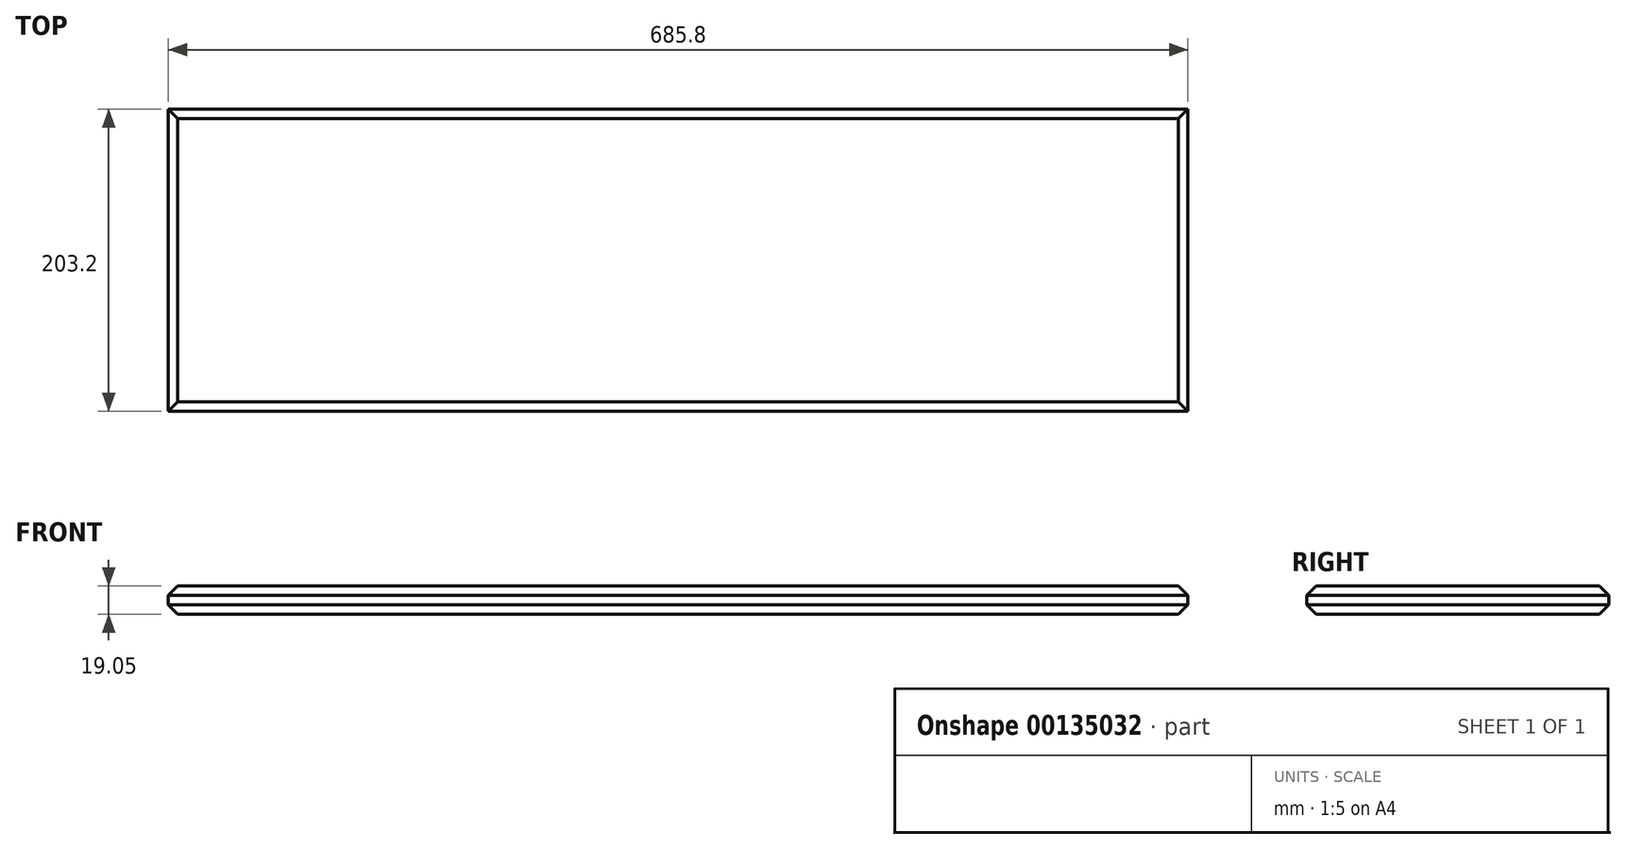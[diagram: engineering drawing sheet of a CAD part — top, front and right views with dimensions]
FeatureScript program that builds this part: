
annotation { "Feature Type Name" : "Feature", "Feature Type Description" : "" }
export const myFeature = defineFeature(function(context is Context, id is Id, definition is map)
    precondition{}
    {
        {
            var Q0;
            Q0=qCreatedBy(makeId("Top.planeOp"),FACE);
            var sketch = newSketch(context, id + "F0", { "sketchPlane" : qUnion([Q0])});
            skLineSegment(sketch, "E0.bottom", {"start": v(-467.83, 102.3) * mm, "end": v(217.97, 102.3) * mm});
            skLineSegment(sketch, "E0.top", {"start": v(-467.83, -100.9) * mm, "end": v(217.97, -100.9) * mm});
            skLineSegment(sketch, "E0.left", {"start": v(-467.83, 102.3) * mm, "end": v(-467.83, -100.9) * mm});
            skLineSegment(sketch, "E0.right", {"start": v(217.97, 102.3) * mm, "end": v(217.97, -100.9) * mm});
            skSolve(sketch);
        }
        {
            var Q0;
            Q0=makeQuery(id+"F0.imprint","IMPRINT",FACE,{"disambiguationData":[TD([[makeQuery(id+"F0.imprint","IMPRINT",EDGE,{"derivedFrom":sQuery(id+"F0.wireOp",EDGE,"E0.bottom")}),-1.0]])]});
            extrude(context, id + "F1", {"entities" : qUnion([Q0]), "depth" : 19.05 * mm});
        }
        {
            var Q0;
            Q0=makeQuery(id+"F1.opExtrude","CAP_FACE",FACE,{"disambiguationData":[OSD([sQuery(id+"F0.wireOp",EDGE,"E0.bottom"),sQuery(id+"F0.wireOp",EDGE,"E0.top"),sQuery(id+"F0.wireOp",EDGE,"E0.left"),sQuery(id+"F0.wireOp",EDGE,"E0.right")])],"isStart":false});
            chamfer(context, id + "F2", {"entities" : qUnion([Q0]), "width" : 6.35 * mm, "tangentPropagation" : true});
        }
        {
            var Q0;
            Q0=makeQuery(id+"F1.opExtrude","CAP_FACE",FACE,{"disambiguationData":[OSD([sQuery(id+"F0.wireOp",EDGE,"E0.bottom"),sQuery(id+"F0.wireOp",EDGE,"E0.top"),sQuery(id+"F0.wireOp",EDGE,"E0.left"),sQuery(id+"F0.wireOp",EDGE,"E0.right")])],"isStart":true});
            chamfer(context, id + "F3", {"entities" : qUnion([Q0]), "width" : 6.35 * mm, "tangentPropagation" : true});
        }
    });
